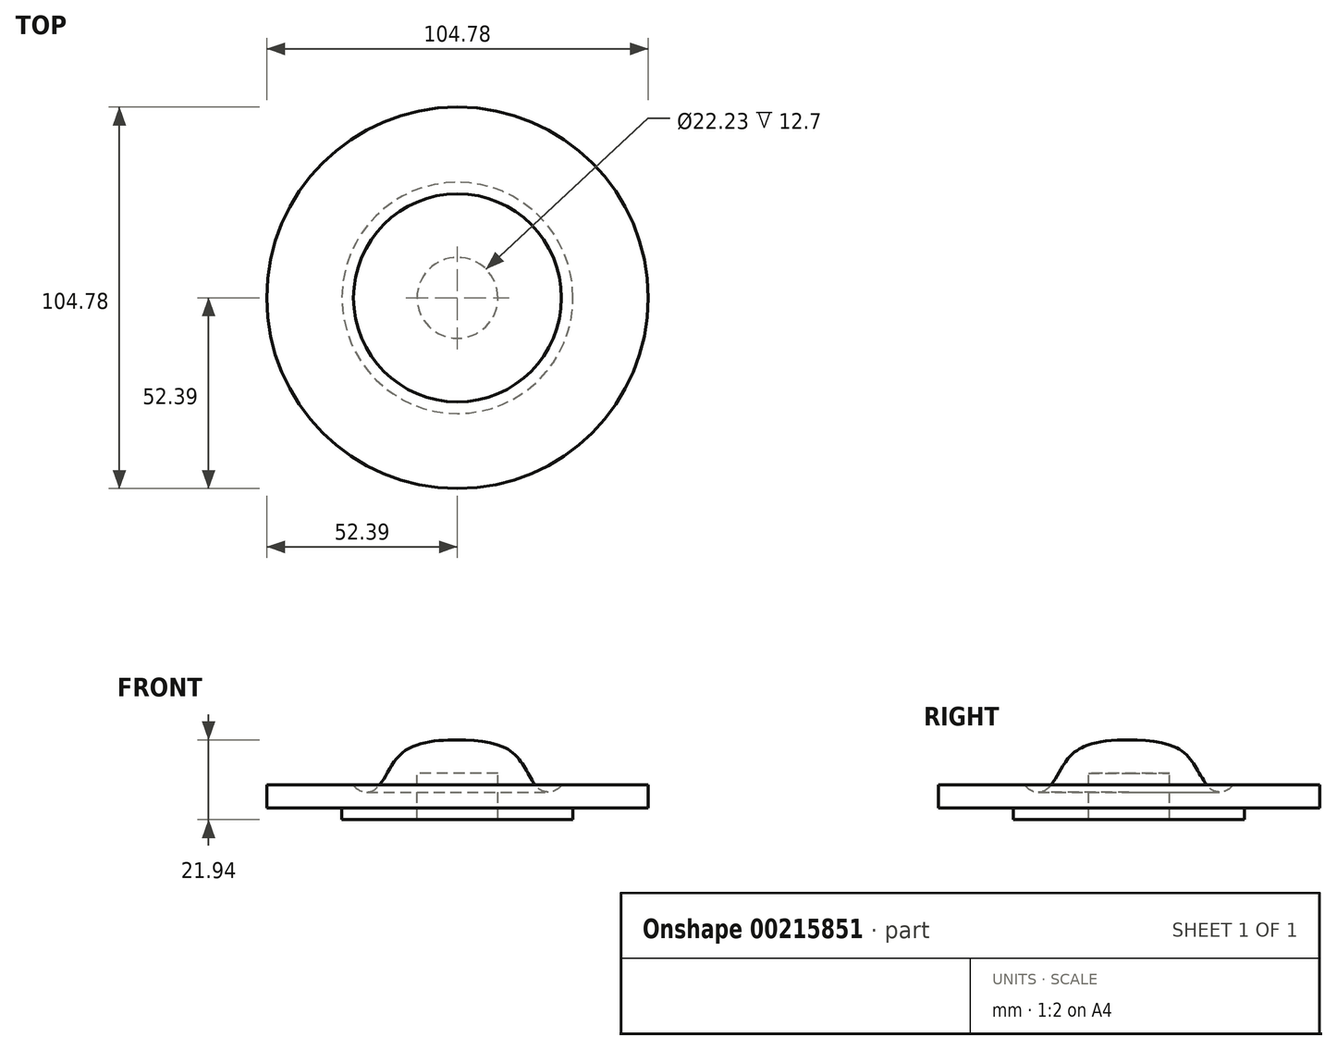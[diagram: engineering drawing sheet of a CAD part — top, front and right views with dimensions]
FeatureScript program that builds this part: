
annotation { "Feature Type Name" : "Feature", "Feature Type Description" : "" }
export const myFeature = defineFeature(function(context is Context, id is Id, definition is map)
    precondition{}
    {
        {
            var Q0;
            Q0=qCreatedBy(makeId("Front.planeOp"),FACE);
            var sketch = newSketch(context, id + "F0", { "sketchPlane" : qUnion([Q0])});
            skLineSegment(sketch, "E0", {"start": v(0, 12.7) * mm, "end": v(-11.11, 12.7) * mm});
            skLineSegment(sketch, "E1", {"start": v(-11.11, 12.7) * mm, "end": v(-11.11, 0) * mm});
            skLineSegment(sketch, "E2", {"start": v(-11.11, 0) * mm, "end": v(-31.75, 0) * mm});
            skLineSegment(sketch, "E3", {"start": v(-31.75, 0) * mm, "end": v(-31.75, 3.18) * mm});
            skLineSegment(sketch, "E4", {"start": v(-31.75, 3.18) * mm, "end": v(-52.39, 3.17) * mm});
            skLineSegment(sketch, "E5", {"start": v(-52.39, 3.17) * mm, "end": v(-52.39, 9.52) * mm});
            skLineSegment(sketch, "E6", {"start": v(-52.39, 9.52) * mm, "end": v(-28.58, 9.52) * mm});
            skFitSpline(sketch, "E7", {"points": [v(-28.57, 9.52) * mm, v(-22.93, 8.13) * mm, v(-15.68, 17.95) * mm, v(0, 21.94) * mm], "startDerivative": vector(15.96, -22.47) * mm, "endDerivative": vector(42.82, 0) * mm});
            skLineSegment(sketch, "E8", {"start": v(0, 21.94) * mm, "end": v(0, 12.7) * mm});
            skSolve(sketch);
        }
        {
            var Q0;
            Q0=qSketchRegion(id+"F0",true);
            var Q1;
            Q1=sQuery(id+"F0.wireOp",EDGE,"E8");
            revolve(context, id + "F1", {"entities" : qUnion([Q0]), "axis" : qUnion([Q1]), "revolveType" : RevolveType.FULL});
        }
    });
